# Revit family: 306_R7_R-B_
name_source: partatom
category: Pipe Accessories
units: mm (PartAtom-declared; Revit-internal decimal feet)

## family parameters
Always vertical = Yes
Cut with Voids When Loaded = No
Part Type = Valve - Breaks Into
Round Connector Dimension = Use Diameter
Shared = No
Work Plane-Based = No

## types (8) — shared parameters
B33 = 4 mm  [stored 0.0131234 ft]
B4 = 11 mm
BB = 23 mm
CAT0 = Yes
Description = Characterised control valve, 3-way, Flange, PN 6
H2 = 8 mm  [stored 0.0262467 ft]
L2D_Min = 3048 mm
Manufacturer = Belimo
QmdConnectorList = 301;D;302;D;303;D
magiPartTypeId = 306
magiProductFamilyId = R7*R-B*
zero-valued in all types: MC_Default_elevation

## per-type parameters (varying)
| type | C | C1 | C1__ve | C2 | C__ve | D | FD1 | FD2 | FD3 | FD4 | H | H1 | H11 | H1__ve | L2D | LL | M | M1 | M1__ve | W2D |
| R7015RP63-B1 | 10 mm  [stored 0.0328084 ft] | 3 mm  [stored 0.00984252 ft] | -3 mm | 74 mm | -10 mm  [stored -0.0328084 ft] | 15 mm | 40 mm | 16 mm  [stored 0.0524934 ft] | 20 mm  [stored 0.0656168 ft] | 10 mm  [stored 0.0328084 ft] | 35 mm  [stored 0.114829 ft] | 4 mm  [stored 0.0131234 ft] | 31 mm | -4 mm  [stored -0.0131234 ft] | 101 mm | 51 mm | 73 mm | 60 mm | -60 mm | 15 mm  [stored 0.0492126 ft] |
| R7050R25-B3 | 12 mm  [stored 0.0393701 ft] | 4 mm  [stored 0.0131234 ft] | -4 mm  [stored -0.0131234 ft] | 133 mm | -12 mm  [stored -0.0393701 ft] | 50 mm | 70 mm | 28 mm  [stored 0.0918635 ft] | 35 mm  [stored 0.114829 ft] | 18 mm  [stored 0.0590551 ft] | 56 mm | 7 mm  [stored 0.0229659 ft] | 49 mm | -7 mm  [stored -0.0229659 ft] | 165 mm | 83 mm | 121 mm | 105 mm | -105 mm  [stored -0.344488 ft] | 50 mm |
| R7040R16-B3 | 12 mm  [stored 0.0393701 ft] | 4 mm  [stored 0.0131234 ft] | -4 mm  [stored -0.0131234 ft] | 119 mm | -12 mm  [stored -0.0393701 ft] | 40 mm | 65 mm | 26 mm  [stored 0.0853018 ft] | 33 mm | 16 mm  [stored 0.0524934 ft] | 51 mm | 6 mm  [stored 0.019685 ft] | 44 mm | -6 mm | 151 mm | 76 mm | 105 mm | 89 mm | -89 mm  [stored -0.291995 ft] | 40 mm |
| R7032R16-B3 | 12 mm  [stored 0.0393701 ft] | 4 mm  [stored 0.0131234 ft] | -4 mm  [stored -0.0131234 ft] | 111 mm | -12 mm  [stored -0.0393701 ft] | 32 mm | 60 mm | 24 mm  [stored 0.0787402 ft] | 30 mm  [stored 0.0984252 ft] | 15 mm  [stored 0.0492126 ft] | 51 mm | 6 mm  [stored 0.019685 ft] | 44 mm | -6 mm | 143 mm | 72 mm | 103 mm | 87 mm | -87 mm | 32 mm  [stored 0.104987 ft] |
| R7025R10-B2 | 15 mm  [stored 0.0492126 ft] | 5 mm  [stored 0.0164042 ft] | -5 mm  [stored -0.0164042 ft] | 92 mm | -15 mm  [stored -0.0492126 ft] | 25 mm | 50 mm | 20 mm  [stored 0.0656168 ft] | 25 mm  [stored 0.082021 ft] | 13 mm | 46 mm | 6 mm  [stored 0.019685 ft] | 40 mm | -6 mm | 132 mm | 66 mm | 92 mm | 72 mm | -72 mm  [stored -0.23622 ft] | 25 mm  [stored 0.082021 ft] |
| R7020R6P3-B1 | 10 mm  [stored 0.0328084 ft] | 3 mm  [stored 0.00984252 ft] | -3 mm | 85 mm | -10 mm  [stored -0.0328084 ft] | 20 mm | 45 mm | 18 mm  [stored 0.0590551 ft] | 23 mm | 11 mm | 46 mm | 6 mm  [stored 0.019685 ft] | 40 mm | -6 mm | 112 mm | 56 mm | 80 mm | 67 mm | -67 mm | 20 mm  [stored 0.0656168 ft] |
| R7015R4-B1 | 10 mm  [stored 0.0328084 ft] | 3 mm  [stored 0.00984252 ft] | -3 mm | 74 mm | -10 mm  [stored -0.0328084 ft] | 15 mm | 40 mm | 16 mm  [stored 0.0524934 ft] | 20 mm  [stored 0.0656168 ft] | 10 mm  [stored 0.0328084 ft] | 44 mm | 6 mm  [stored 0.019685 ft] | 39 mm | -6 mm | 101 mm | 51 mm | 73 mm | 60 mm | -60 mm | 15 mm  [stored 0.0492126 ft] |
| R7015R1P6-B1 | 10 mm  [stored 0.0328084 ft] | 3 mm  [stored 0.00984252 ft] | -3 mm | 74 mm | -10 mm  [stored -0.0328084 ft] | 15 mm | 40 mm | 16 mm  [stored 0.0524934 ft] | 20 mm  [stored 0.0656168 ft] | 10 mm  [stored 0.0328084 ft] | 35 mm  [stored 0.114829 ft] | 4 mm  [stored 0.0131234 ft] | 31 mm | -4 mm  [stored -0.0131234 ft] | 101 mm | 51 mm | 73 mm | 60 mm | -60 mm | 15 mm  [stored 0.0492126 ft] |

note: column(s) folded — value = type name in every type: magiProductCode, magiProductId

note: [stored X ft] marks values corroborated as IEEE doubles in the binary element streams (Revit-internal decimal feet)

## geometry (parser evidence)
native form markers: Sweep x2
no freeform markers — native parametric forms only
